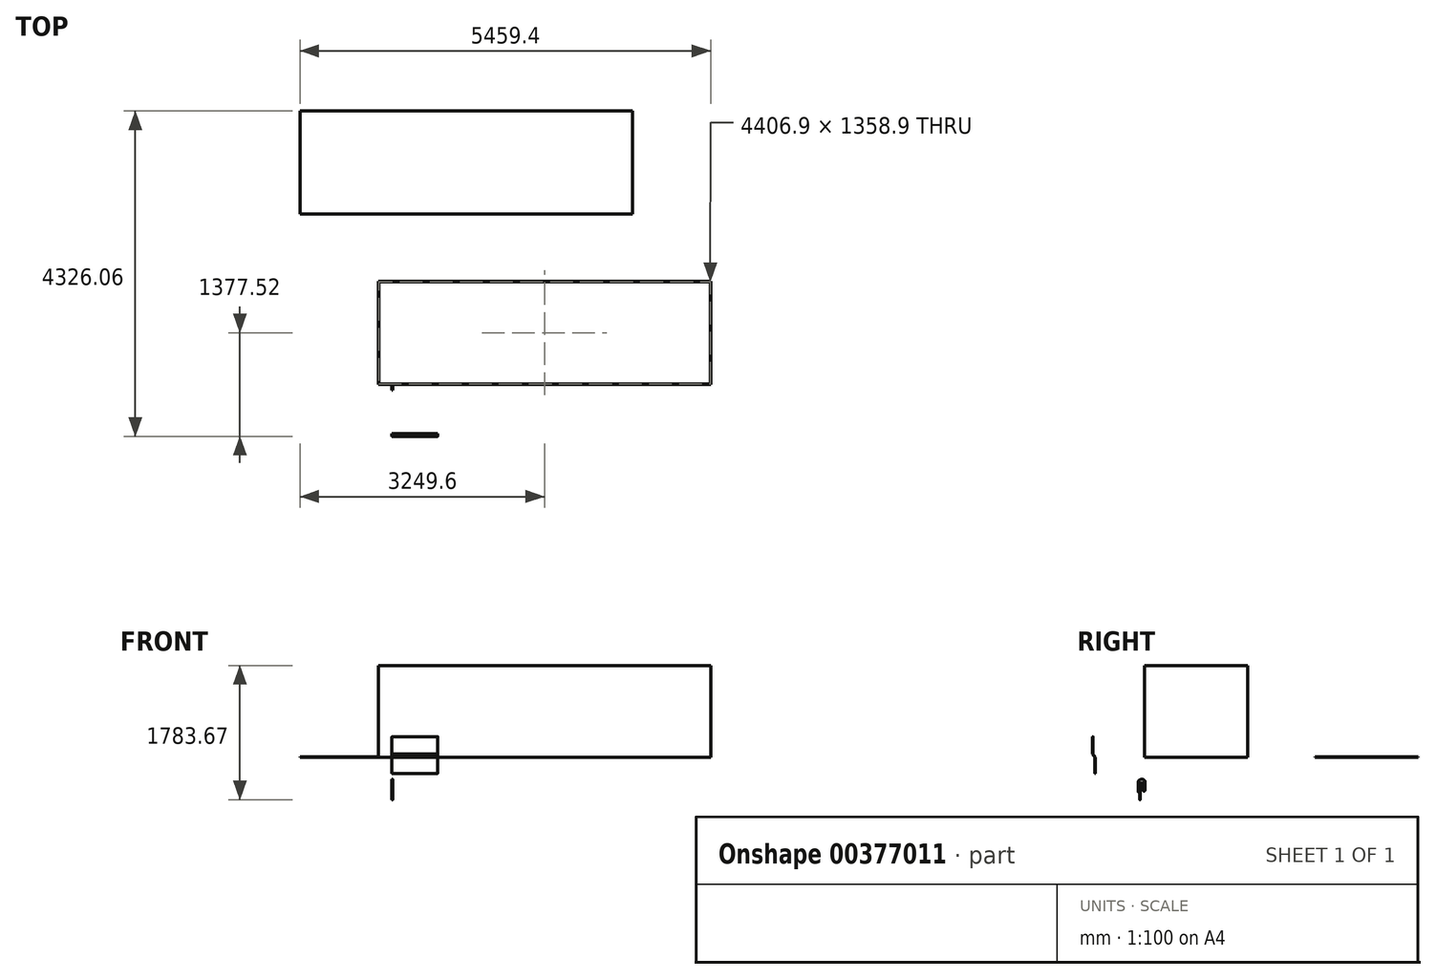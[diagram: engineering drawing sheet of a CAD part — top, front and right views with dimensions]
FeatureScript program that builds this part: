
annotation { "Feature Type Name" : "Feature", "Feature Type Description" : "" }
export const myFeature = defineFeature(function(context is Context, id is Id, definition is map)
    precondition{}
    {
        {
            var Q0;
            Q0=qCreatedBy(makeId("Top.planeOp"),FACE);
            var sketch = newSketch(context, id + "F0", { "sketchPlane" : qUnion([Q0])});
            skLineSegment(sketch, "E0", {"start": v(-180.44, 1218.23) * mm, "end": v(-180.44, -153.37) * mm});
            skLineSegment(sketch, "E1", {"start": v(-180.44, -153.37) * mm, "end": v(4239.16, -153.37) * mm});
            skLineSegment(sketch, "E2", {"start": v(4239.16, -153.37) * mm, "end": v(4239.16, 1218.23) * mm});
            skLineSegment(sketch, "E3", {"start": v(4239.16, 1218.23) * mm, "end": v(-180.44, 1218.23) * mm});
            skLineSegment(sketch, "E4.0", {"start": v(-174.1, -147.02) * mm, "end": v(4232.8, -147.02) * mm});
            skLineSegment(sketch, "E5.0", {"start": v(4232.8, -147.02) * mm, "end": v(4232.8, 1211.88) * mm});
            skLineSegment(sketch, "E6.0", {"start": v(4232.8, 1211.88) * mm, "end": v(-174.1, 1211.88) * mm});
            skLineSegment(sketch, "E7", {"start": v(-174.1, 1211.88) * mm, "end": v(-174.1, -147.02) * mm});
            skSolve(sketch);
        }
        {
            var Q0;
            Q0 = qSketchRegion(id + "F0", true);
            extrude(context, id + "F1", {"entities" : qUnion([Q0]), "depth" : 1219.2 * mm});
        }
        {
            var Q0;
            Q0=qCreatedBy(makeId("Top.planeOp"),FACE);
            var sketch = newSketch(context, id + "F2", { "sketchPlane" : qUnion([Q0])});
            skLineSegment(sketch, "E8.bottom", {"start": v(3199.36, 3480.97) * mm, "end": v(-1220.24, 3480.97) * mm});
            skLineSegment(sketch, "E8.top", {"start": v(3199.36, 2109.37) * mm, "end": v(-1220.24, 2109.37) * mm});
            skLineSegment(sketch, "E8.left", {"start": v(3199.36, 3480.97) * mm, "end": v(3199.36, 2109.37) * mm});
            skLineSegment(sketch, "E8.right", {"start": v(-1220.24, 3480.97) * mm, "end": v(-1220.24, 2109.37) * mm});
            skPoint(sketch, "E8.middle", {"position": v(989.56, 2795.17) * mm});
            skSolve(sketch);
        }
        {
            var Q0;
            Q0 = qSketchRegion(id + "F2", true);
            extrude(context, id + "F3", {"entities" : qUnion([Q0]), "operationType" : NewBodyOperationType.ADD, "depth" : 6.35 * mm});
        }
        {
            var Q0;
            Q0=qCreatedBy(makeId("Right.planeOp"),FACE);
            var sketch = newSketch(context, id + "F4", { "sketchPlane" : qUnion([Q0])});
            skLineSegment(sketch, "E9", {"start": v(-815.82, -214.38) * mm, "end": v(-815.82, 0) * mm});
            skLineSegment(sketch, "E10", {"start": v(-815.82, 0) * mm, "end": v(-845.09, 44.45) * mm});
            skLineSegment(sketch, "E11", {"start": v(-845.09, 44.45) * mm, "end": v(-845.09, 271.53) * mm});
            skLineSegment(sketch, "E12.0", {"start": v(-840.26, 45.9) * mm, "end": v(-840.26, 271.53) * mm});
            skLineSegment(sketch, "E12.1", {"start": v(-811, 1.45) * mm, "end": v(-840.26, 45.9) * mm});
            skLineSegment(sketch, "E12.2", {"start": v(-811, -214.38) * mm, "end": v(-811, 1.45) * mm});
            skLineSegment(sketch, "E13", {"start": v(-841.78, 273.05) * mm, "end": v(-843.56, 273.05) * mm});
            skLineSegment(sketch, "E14", {"start": v(-812.52, -215.9) * mm, "end": v(-814.3, -215.9) * mm});
            skPoint(sketch, "E15.visualSharp", {"position": v(-815.82, -215.9) * mm});
            skArc(sketch, "E15.filletArc", {"start": v(-815.82, -214.38) * mm, "mid": v(-815.37, -215.45) * mm, "end": v(-814.3, -215.9) * mm});
            skPoint(sketch, "E16.visualSharp", {"position": v(-811, -215.9) * mm});
            skArc(sketch, "E16.filletArc", {"start": v(-812.52, -215.9) * mm, "mid": v(-811.44, -215.45) * mm, "end": v(-811, -214.38) * mm});
            skPoint(sketch, "E17.visualSharp", {"position": v(-845.09, 273.05) * mm});
            skArc(sketch, "E17.filletArc", {"start": v(-843.56, 273.05) * mm, "mid": v(-844.64, 272.6) * mm, "end": v(-845.09, 271.53) * mm});
            skPoint(sketch, "E18.visualSharp", {"position": v(-840.26, 273.05) * mm});
            skArc(sketch, "E18.filletArc", {"start": v(-840.26, 271.53) * mm, "mid": v(-840.7, 272.6) * mm, "end": v(-841.78, 273.05) * mm});
            skSolve(sketch);
        }
        {
            var Q0;
            Q0 = qSketchRegion(id + "F4", true);
            extrude(context, id + "F5", {"entities" : qUnion([Q0]), "depth" : 609.6 * mm});
        }
        {
            var Q0;
            Q0=qCreatedBy(makeId("Right.planeOp"),FACE);
            var sketch = newSketch(context, id + "F6", { "sketchPlane" : qUnion([Q0])});
            skLineSegment(sketch, "E19", {"start": v(-148.93, -442.8) * mm, "end": v(-148.93, -442.8) * mm});
            skLineSegment(sketch, "E20", {"start": v(-221, -564.47) * mm, "end": v(-211.92, -564.47) * mm});
            skLineSegment(sketch, "E21", {"start": v(-210.9, -563.46) * mm, "end": v(-210.9, -347.56) * mm});
            skLineSegment(sketch, "E22", {"start": v(-204.56, -341.2) * mm, "end": v(-179.16, -341.2) * mm});
            skLineSegment(sketch, "E23", {"start": v(-172.8, -347.56) * mm, "end": v(-172.8, -442.8) * mm});
            skLineSegment(sketch, "E24", {"start": v(-166.46, -449.16) * mm, "end": v(-155.28, -449.16) * mm});
            skArc(sketch, "E25.filletArc", {"start": v(-155.28, -449.16) * mm, "mid": v(-150.79, -447.3) * mm, "end": v(-148.93, -442.8) * mm});
            skArc(sketch, "E26.filletArc", {"start": v(-172.8, -442.8) * mm, "mid": v(-170.95, -447.3) * mm, "end": v(-166.46, -449.16) * mm});
            skLineSegment(sketch, "E27", {"start": v(-148.93, -341.2) * mm, "end": v(-148.93, -341.2) * mm});
            skPoint(sketch, "E28.visualSharp", {"position": v(-210.9, -564.47) * mm});
            skArc(sketch, "E28.filletArc", {"start": v(-211.92, -564.47) * mm, "mid": v(-211.2, -564.17) * mm, "end": v(-210.9, -563.46) * mm});
            skLineSegment(sketch, "E29", {"start": v(-222.02, -563.46) * mm, "end": v(-222.02, -471.3) * mm});
            skLineSegment(sketch, "E30", {"start": v(-225.2, -468.13) * mm, "end": v(-231.83, -468.13) * mm});
            skLineSegment(sketch, "E31", {"start": v(-235, -464.95) * mm, "end": v(-235, -315.73) * mm});
            skPoint(sketch, "E32.visualSharp", {"position": v(-222.02, -468.13) * mm});
            skArc(sketch, "E32.filletArc", {"start": v(-222.02, -471.3) * mm, "mid": v(-222.95, -469.06) * mm, "end": v(-225.2, -468.13) * mm});
            skPoint(sketch, "E33.visualSharp", {"position": v(-235, -468.13) * mm});
            skArc(sketch, "E33.filletArc", {"start": v(-235, -464.95) * mm, "mid": v(-234.08, -467.2) * mm, "end": v(-231.83, -468.13) * mm});
            skArc(sketch, "E34.filletArc", {"start": v(-172.8, -347.56) * mm, "mid": v(-174.67, -343.07) * mm, "end": v(-179.16, -341.2) * mm});
            skArc(sketch, "E35", {"start": v(-148.93, -315.78) * mm, "mid": v(-191.96, -293.39) * mm, "end": v(-235, -315.73) * mm});
            skPoint(sketch, "E36.visualSharp", {"position": v(-210.9, -341.2) * mm});
            skArc(sketch, "E36.filletArc", {"start": v(-204.56, -341.2) * mm, "mid": v(-209.05, -343.07) * mm, "end": v(-210.9, -347.56) * mm});
            skLineSegment(sketch, "E37", {"start": v(-148.93, -341.2) * mm, "end": v(-148.93, -315.78) * mm});
            skLineSegment(sketch, "E38", {"start": v(-148.93, -442.8) * mm, "end": v(-148.93, -341.2) * mm});
            skArc(sketch, "E39.filletArc", {"start": v(-222.02, -563.46) * mm, "mid": v(-221.72, -564.17) * mm, "end": v(-221, -564.47) * mm});
            skSolve(sketch);
        }
        {
            var Q0;
            Q0 = qSketchRegion(id + "F6", true);
            extrude(context, id + "F7", {"entities" : qUnion([Q0]), "depth" : 12.7 * mm});
        }
    });
